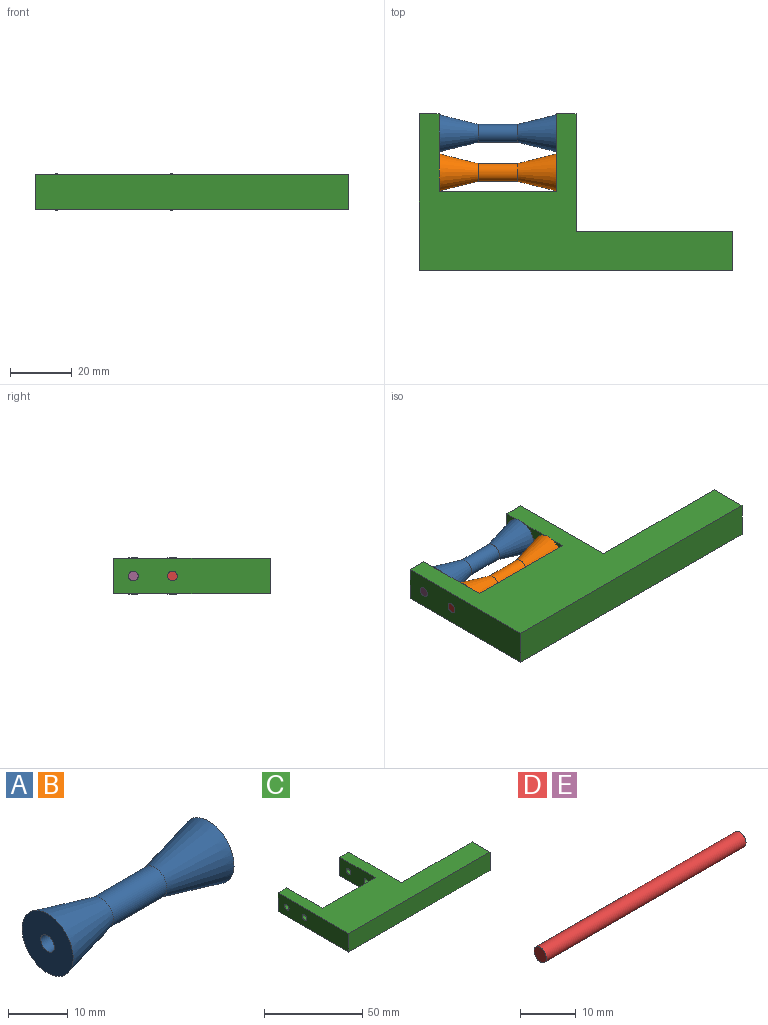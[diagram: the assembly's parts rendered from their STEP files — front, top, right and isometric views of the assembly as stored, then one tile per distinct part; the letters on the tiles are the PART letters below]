
ASSEMBLY  parts=5 mates=4
PART A: 6 faces, bbox 38.1x12.1x12.1 mm
  f0: plane 12.11x12.11mm, normal (1,0,0), area 107mm2, adj f1,f5
  f1: cylinder r=1.61mm len=38.1mm, axis (-1,0,0), area 385mm2, adj f0,f2
  f2: plane 12.11x12.11mm, normal (-1,0,0), area 107mm2, adj f1,f3
  f3: cone r=6.05mm half-angle=14deg, axis (-1,0,0), area 367.3mm2, adj f2,f4
  f4: cylinder r=2.88mm len=12.7mm, axis (-1,0,0), area 229.7mm2, adj f3,f5
  f5: cone r=2.88mm half-angle=14deg, axis (1,0,0), area 367.3mm2, adj f0,f4
PART B: same geometry as A
PART C: 16 faces, bbox 101.6x50.8x11.4 mm
  f0: plane 101.6x11.43mm, normal (0,-1,0), area 1161.3mm2, adj f1,f9,f10,f11
  f1: plane 12.7x11.43mm, normal (1,0,0), area 145.2mm2, adj f0,f2,f10,f11
  f2: plane 50.8x11.43mm, normal (0,1,0), area 580.6mm2, adj f1,f3,f10,f11
  f3: plane 38.1x11.43mm, normal (1,0,0), area 419.6mm2, adj f2,f4,f10,f11,f14,f15
  f4: plane 11.43x6.35mm, normal (0,1,0), area 72.6mm2, adj f3,f5,f10,f11
  f5: plane 25.4x11.43mm, normal (-1,0,0), area 274.5mm2, adj f4,f6,f10,f11,f14,f15
  f6: plane 38.1x11.43mm, normal (0,1,0), area 435.5mm2, adj f5,f7,f10,f11
  f7: plane 25.4x11.43mm, normal (1,0,0), area 274.5mm2, adj f6,f8,f10,f11,f12,f13
  f8: plane 11.43x6.35mm, normal (0,1,0), area 72.6mm2, adj f7,f9,f10,f11
  f9: plane 50.8x11.43mm, normal (-1,0,0), area 564.8mm2, adj f0,f8,f10,f11,f12,f13
  f10: plane 101.6x50.8mm, normal (0,0,1), area 2258.1mm2, adj f0,f1,f2,f3,f4,f5,f6,f7
  f11: plane 101.6x50.8mm, normal (0,0,-1), area 2258.1mm2, adj f0,f1,f2,f3,f4,f5,f6,f7
  f12: cylinder r=1.59mm len=6.35mm, axis (1,0,0), area 63.3mm2, adj f7,f9
  f13: cylinder r=1.59mm len=6.35mm, axis (1,0,0), area 63.3mm2, adj f7,f9
  f14: cylinder r=1.59mm len=6.35mm, axis (1,0,0), area 63.3mm2, adj f3,f5
  f15: cylinder r=1.59mm len=6.35mm, axis (1,0,0), area 63.3mm2, adj f3,f5
PART D: 3 faces, bbox 50.8x3.2x3.2 mm
  f0: cylinder r=1.59mm len=50.8mm, axis (-1,0,0), area 506.7mm2, adj f1,f2
  f1: plane 3.18x3.18mm, normal (1,0,0), area 7.9mm2, adj f0
  f2: plane 3.18x3.18mm, normal (-1,0,0), area 7.9mm2, adj f0
PART E: same geometry as D
PLACE A rot(axis=(0,1,0),180deg) t=(-3.68,36.98,49.92)mm
PLACE B t=(-41.78,24.28,49.92)mm
PLACE C t=(53.47,24.73,44.2)mm
PLACE D t=(-48.13,12.03,44.2)mm
PLACE E rot(axis=(0,0,1),180deg) t=(2.67,113.63,44.2)mm
MATE revolute A.f1 <-> E.f0  axis (-1,0,0) through (-41.78,69.18,49.92)mm
MATE fastened C.f13 <-> D.f0  axis (1,0,0) through (2.67,56.48,49.92)mm
MATE fastened C.f12 <-> E.f0  axis (1,0,0) through (2.67,69.18,49.92)mm
MATE revolute D.f0 <-> B.f1  axis (-1,0,0) through (-22.73,56.48,49.92)mm
